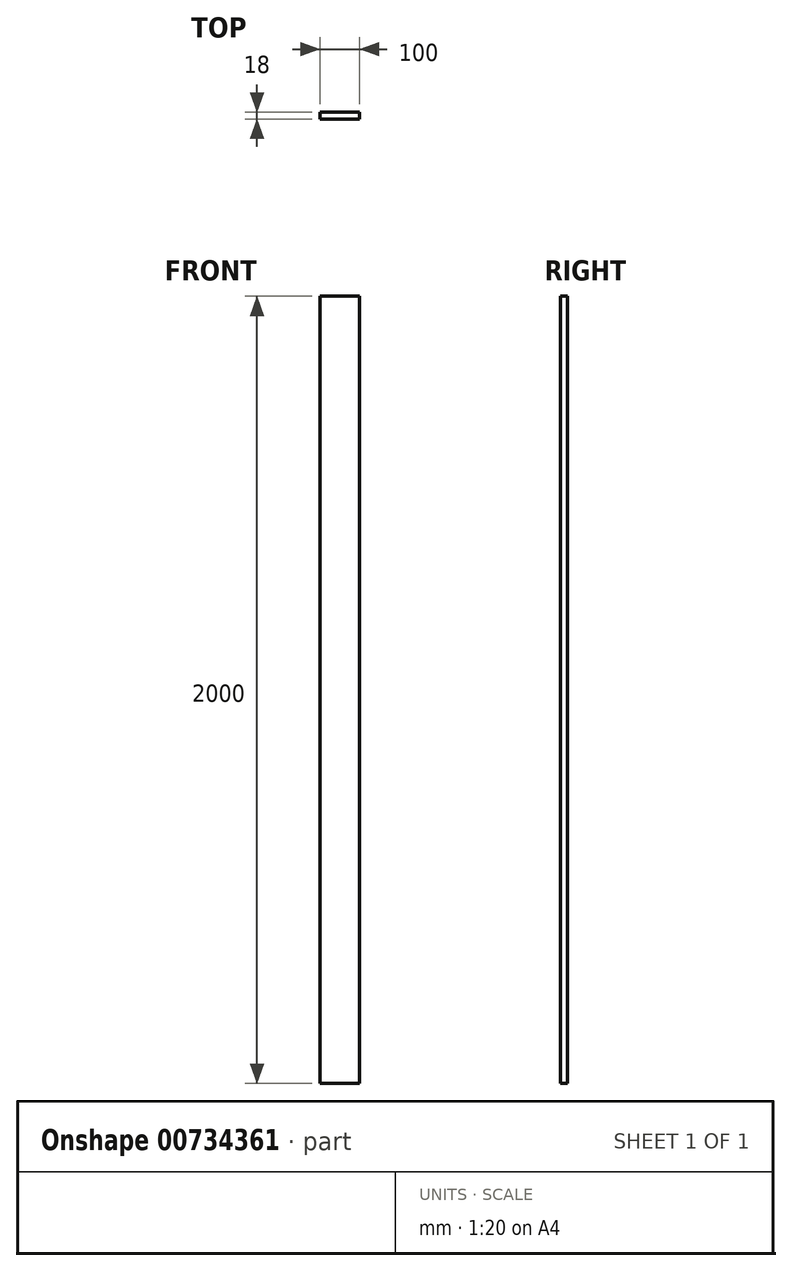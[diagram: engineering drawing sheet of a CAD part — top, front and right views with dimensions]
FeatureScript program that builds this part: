
annotation { "Feature Type Name" : "Feature", "Feature Type Description" : "" }
export const myFeature = defineFeature(function(context is Context, id is Id, definition is map)
    precondition{}
    {
        {
            var Q0;
            Q0=qCreatedBy(makeId("Front.planeOp"),FACE);
            var sketch = newSketch(context, id + "F0", { "sketchPlane" : qUnion([Q0])});
            skLineSegment(sketch, "E0.bottom", {"start": v(-50, -1000) * mm, "end": v(50, -1000) * mm});
            skLineSegment(sketch, "E0.top", {"start": v(-50, 1000) * mm, "end": v(50, 1000) * mm});
            skLineSegment(sketch, "E0.left", {"start": v(-50, -1000) * mm, "end": v(-50, 1000) * mm});
            skLineSegment(sketch, "E0.right", {"start": v(50, -1000) * mm, "end": v(50, 1000) * mm});
            skPoint(sketch, "E0.middle", {"position": v(0, 0) * mm});
            skSolve(sketch);
        }
        {
            var Q0;
            Q0 = qSketchRegion(id + "F0", true);
            extrude(context, id + "F1", {"entities" : qUnion([Q0]), "oppositeDirection" : true, "depth" : 18 * mm, "offsetDistance" : 25 * mm});
        }
    });
